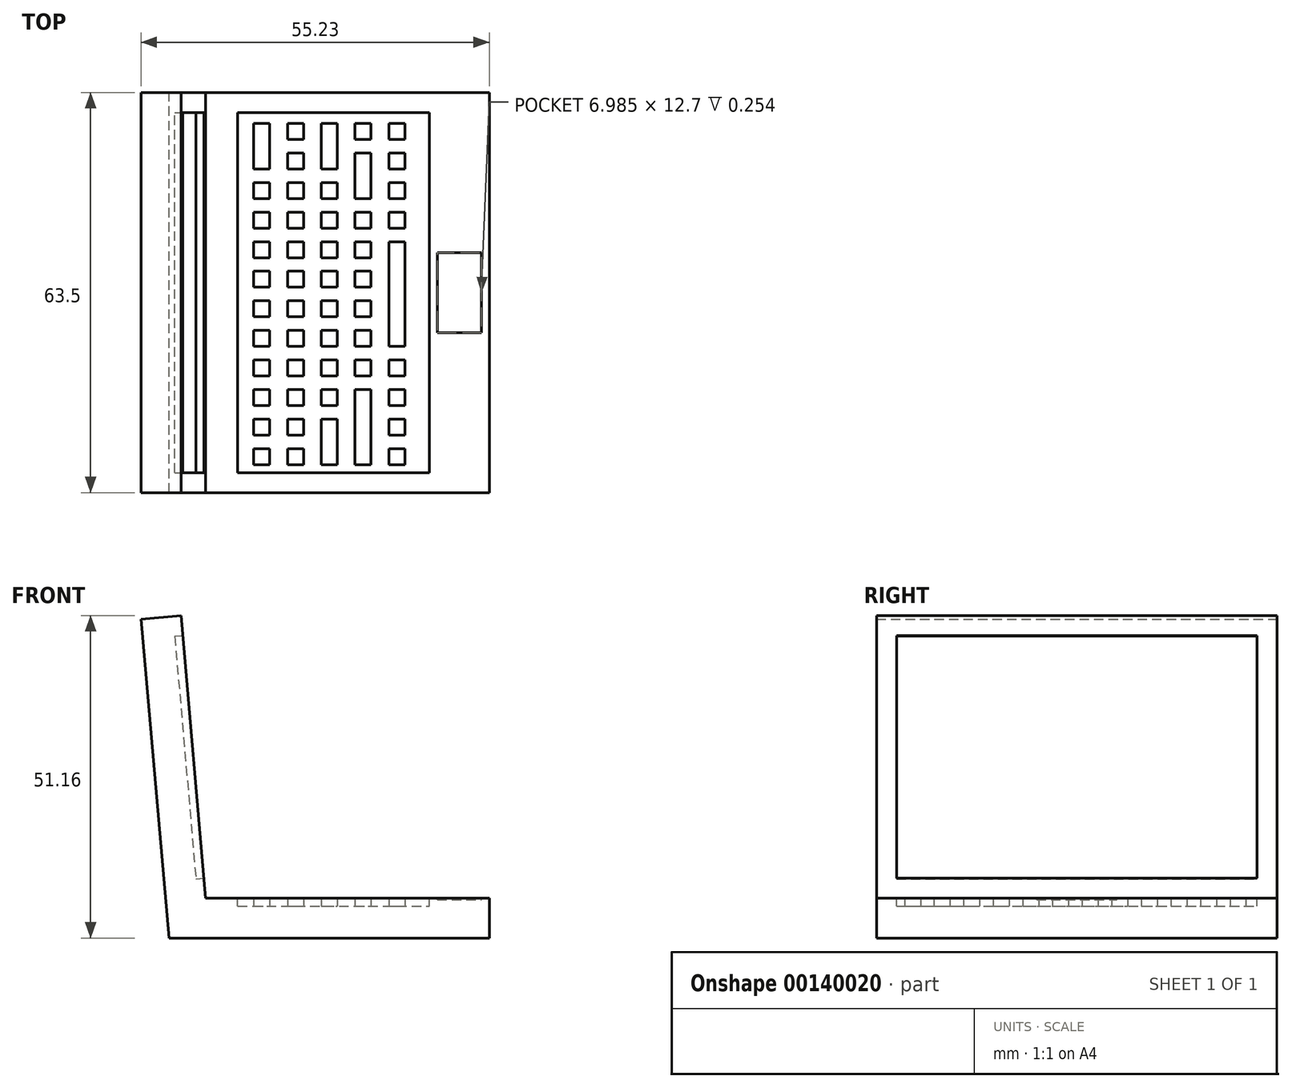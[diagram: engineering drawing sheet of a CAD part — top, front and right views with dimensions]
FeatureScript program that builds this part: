
annotation { "Feature Type Name" : "Feature", "Feature Type Description" : "" }
export const myFeature = defineFeature(function(context is Context, id is Id, definition is map)
    precondition{}
    {
        {
            var Q0;
            Q0=qCreatedBy(makeId("Front.planeOp"),FACE);
            var sketch = newSketch(context, id + "F0", { "sketchPlane" : qUnion([Q0])});
            skLineSegment(sketch, "E0", {"start": v(-10.25, 44.26) * mm, "end": v(-5.82, -6.35) * mm});
            skLineSegment(sketch, "E1", {"start": v(-5.82, -6.35) * mm, "end": v(44.98, -6.35) * mm});
            skLineSegment(sketch, "E2", {"start": v(44.98, -6.35) * mm, "end": v(44.98, 0) * mm});
            skLineSegment(sketch, "E3", {"start": v(44.98, 0) * mm, "end": v(0, 0) * mm});
            skLineSegment(sketch, "E4", {"start": v(0, 0) * mm, "end": v(-3.92, 44.81) * mm});
            skLineSegment(sketch, "E5", {"start": v(-3.92, 44.81) * mm, "end": v(-10.25, 44.26) * mm});
            skSolve(sketch);
        }
        {
            var Q0;
            Q0=makeQuery(id+"F0.imprint","IMPRINT",FACE,{"disambiguationData":[TD([[makeQuery(id+"F0.imprint","IMPRINT",EDGE,{"derivedFrom":sQuery(id+"F0.wireOp",EDGE,"E0")}),1.0]])]});
            extrude(context, id + "F1", {"entities" : qUnion([Q0]), "depth" : 31.75 * mm, "hasSecondDirection" : true, "secondDirectionOppositeDirection" : true, "secondDirectionDepth" : 31.75 * mm});
        }
        {
            var Q0;
            Q0=makeQuery(id+"F1.opExtrude","SWEPT_FACE",FACE,{"disambiguationData":[OSD([sQuery(id+"F0.wireOp",EDGE,"E3")])]});
            var sketch = newSketch(context, id + "F2", { "sketchPlane" : qUnion([Q0])});
            skLineSegment(sketch, "E6.bottom", {"start": v(5.08, -28.57) * mm, "end": v(35.46, -28.57) * mm});
            skLineSegment(sketch, "E6.top", {"start": v(5.08, 28.57) * mm, "end": v(35.46, 28.57) * mm});
            skLineSegment(sketch, "E6.left", {"start": v(5.08, -28.57) * mm, "end": v(5.08, 28.57) * mm});
            skLineSegment(sketch, "E6.right", {"start": v(35.46, -28.57) * mm, "end": v(35.46, 28.57) * mm});
            skPoint(sketch, "E7", {"position": v(5.08, 0) * mm});
            skSolve(sketch);
        }
        {
            var Q0;
            Q0 = qSketchRegion(id + "F2", true);
            extrude(context, id + "F3", {"entities" : qUnion([Q0]), "operationType" : NewBodyOperationType.REMOVE, "oppositeDirection" : true, "depth" : 1.27 * mm});
        }
        {
            var Q0;
            Q0=makeQuery(id+"F1.opExtrude","SWEPT_FACE",FACE,{"disambiguationData":[OSD([sQuery(id+"F0.wireOp",EDGE,"E4")])]});
            var sketch = newSketch(context, id + "F4", { "sketchPlane" : qUnion([Q0])});
            skLineSegment(sketch, "E8.bottom", {"start": v(-28.57, 41.8) * mm, "end": v(28.57, 41.8) * mm});
            skLineSegment(sketch, "E8.top", {"start": v(-28.57, 3.17) * mm, "end": v(28.57, 3.17) * mm});
            skLineSegment(sketch, "E8.left", {"start": v(-28.57, 41.8) * mm, "end": v(-28.57, 3.17) * mm});
            skLineSegment(sketch, "E8.right", {"start": v(28.57, 41.8) * mm, "end": v(28.57, 3.18) * mm});
            skPoint(sketch, "E9", {"position": v(0, 41.8) * mm});
            skSolve(sketch);
        }
        {
            var Q0;
            Q0=makeQuery(id+"F4.imprint","IMPRINT",FACE,{"disambiguationData":[TD([[makeQuery(id+"F4.imprint","IMPRINT",EDGE,{"derivedFrom":sQuery(id+"F4.wireOp",EDGE,"E8.bottom")}),-1.0]])]});
            extrude(context, id + "F5", {"entities" : qUnion([Q0]), "operationType" : NewBodyOperationType.REMOVE, "oppositeDirection" : true, "depth" : 1.27 * mm});
        }
        {
            var Q0;
            Q0=makeQuery(id+"F3.boolean.opBoolean","COPY",FACE,{"derivedFrom":makeQuery(id+"F3.opExtrude","CAP_FACE",FACE,{"disambiguationData":[OSD([sQuery(id+"F2.wireOp",EDGE,"E6.bottom"),sQuery(id+"F2.wireOp",EDGE,"E6.top"),sQuery(id+"F2.wireOp",EDGE,"E6.left"),sQuery(id+"F2.wireOp",EDGE,"E6.right")])],"isStart":false})});
            var sketch = newSketch(context, id + "F6", { "sketchPlane" : qUnion([Q0])});
            skLineSegment(sketch, "E10.bottom", {"start": v(7.62, -27.3) * mm, "end": v(10.16, -27.3) * mm});
            skLineSegment(sketch, "E10.top", {"start": v(7.62, -24.76) * mm, "end": v(10.16, -24.76) * mm});
            skLineSegment(sketch, "E10.left", {"start": v(7.62, -27.3) * mm, "end": v(7.62, -24.76) * mm});
            skLineSegment(sketch, "E10.right", {"start": v(10.16, -27.3) * mm, "end": v(10.16, -24.77) * mm});
            skLineSegment(sketch, "E11.0.1.0", {"start": v(10.16, -22.61) * mm, "end": v(10.16, -20.07) * mm});
            skLineSegment(sketch, "E11.0.1.1", {"start": v(7.62, -22.61) * mm, "end": v(7.62, -20.07) * mm});
            skLineSegment(sketch, "E11.0.1.2", {"start": v(7.62, -20.07) * mm, "end": v(10.16, -20.07) * mm});
            skLineSegment(sketch, "E11.0.1.3", {"start": v(7.62, -22.61) * mm, "end": v(10.16, -22.61) * mm});
            skLineSegment(sketch, "E11.0.2.0", {"start": v(10.16, -17.92) * mm, "end": v(10.16, -15.38) * mm});
            skLineSegment(sketch, "E11.0.2.1", {"start": v(7.62, -17.92) * mm, "end": v(7.62, -15.38) * mm});
            skLineSegment(sketch, "E11.0.2.2", {"start": v(7.62, -15.38) * mm, "end": v(10.16, -15.38) * mm});
            skLineSegment(sketch, "E11.0.2.3", {"start": v(7.62, -17.92) * mm, "end": v(10.16, -17.92) * mm});
            skLineSegment(sketch, "E11.0.3.0", {"start": v(10.16, -13.23) * mm, "end": v(10.16, -10.69) * mm});
            skLineSegment(sketch, "E11.0.3.1", {"start": v(7.62, -13.23) * mm, "end": v(7.62, -10.69) * mm});
            skLineSegment(sketch, "E11.0.3.2", {"start": v(7.62, -10.69) * mm, "end": v(10.16, -10.69) * mm});
            skLineSegment(sketch, "E11.0.3.3", {"start": v(7.62, -13.23) * mm, "end": v(10.16, -13.23) * mm});
            skLineSegment(sketch, "E11.0.4.0", {"start": v(10.16, -8.53) * mm, "end": v(10.16, -6) * mm});
            skLineSegment(sketch, "E11.0.4.1", {"start": v(7.62, -8.53) * mm, "end": v(7.62, -6) * mm});
            skLineSegment(sketch, "E11.0.4.2", {"start": v(7.62, -6) * mm, "end": v(10.16, -6) * mm});
            skLineSegment(sketch, "E11.0.4.3", {"start": v(7.62, -8.53) * mm, "end": v(10.16, -8.53) * mm});
            skLineSegment(sketch, "E11.0.5.0", {"start": v(10.16, -3.84) * mm, "end": v(10.16, -1.3) * mm});
            skLineSegment(sketch, "E11.0.5.1", {"start": v(7.62, -3.84) * mm, "end": v(7.62, -1.3) * mm});
            skLineSegment(sketch, "E11.0.5.2", {"start": v(7.62, -1.3) * mm, "end": v(10.16, -1.3) * mm});
            skLineSegment(sketch, "E11.0.5.3", {"start": v(7.62, -3.84) * mm, "end": v(10.16, -3.84) * mm});
            skLineSegment(sketch, "E11.0.6.0", {"start": v(10.16, 0.85) * mm, "end": v(10.16, 3.4) * mm});
            skLineSegment(sketch, "E11.0.6.1", {"start": v(7.62, 0.85) * mm, "end": v(7.62, 3.4) * mm});
            skLineSegment(sketch, "E11.0.6.2", {"start": v(7.62, 3.4) * mm, "end": v(10.16, 3.4) * mm});
            skLineSegment(sketch, "E11.0.6.3", {"start": v(7.62, 0.85) * mm, "end": v(10.16, 0.85) * mm});
            skLineSegment(sketch, "E11.0.7.0", {"start": v(10.16, 5.54) * mm, "end": v(10.16, 8.08) * mm});
            skLineSegment(sketch, "E11.0.7.1", {"start": v(7.62, 5.54) * mm, "end": v(7.62, 8.08) * mm});
            skLineSegment(sketch, "E11.0.7.2", {"start": v(7.62, 8.08) * mm, "end": v(10.16, 8.08) * mm});
            skLineSegment(sketch, "E11.0.7.3", {"start": v(7.62, 5.54) * mm, "end": v(10.16, 5.54) * mm});
            skLineSegment(sketch, "E11.0.8.0", {"start": v(10.16, 10.24) * mm, "end": v(10.16, 12.78) * mm});
            skLineSegment(sketch, "E11.0.8.1", {"start": v(7.62, 10.24) * mm, "end": v(7.62, 12.78) * mm});
            skLineSegment(sketch, "E11.0.8.2", {"start": v(7.62, 12.78) * mm, "end": v(10.16, 12.78) * mm});
            skLineSegment(sketch, "E11.0.8.3", {"start": v(7.62, 10.24) * mm, "end": v(10.16, 10.24) * mm});
            skLineSegment(sketch, "E11.0.9.0", {"start": v(10.16, 14.93) * mm, "end": v(10.16, 17.47) * mm});
            skLineSegment(sketch, "E11.0.9.1", {"start": v(7.62, 14.93) * mm, "end": v(7.62, 17.47) * mm});
            skLineSegment(sketch, "E11.0.9.2", {"start": v(7.62, 17.47) * mm, "end": v(10.16, 17.47) * mm});
            skLineSegment(sketch, "E11.0.9.3", {"start": v(7.62, 14.93) * mm, "end": v(10.16, 14.93) * mm});
            skLineSegment(sketch, "E11.0.10.0", {"start": v(10.16, 19.62) * mm, "end": v(10.16, 22.16) * mm});
            skLineSegment(sketch, "E11.0.10.1", {"start": v(7.62, 19.62) * mm, "end": v(7.62, 22.16) * mm});
            skLineSegment(sketch, "E11.0.10.3", {"start": v(7.62, 19.62) * mm, "end": v(10.16, 19.62) * mm});
            skLineSegment(sketch, "E11.0.11.0", {"start": v(10.16, 24.31) * mm, "end": v(10.16, 26.85) * mm});
            skLineSegment(sketch, "E11.0.11.1", {"start": v(7.62, 24.31) * mm, "end": v(7.62, 26.85) * mm});
            skLineSegment(sketch, "E11.0.11.2", {"start": v(7.62, 26.85) * mm, "end": v(10.16, 26.85) * mm});
            skLineSegment(sketch, "E11.1.0.0", {"start": v(15.52, -27.3) * mm, "end": v(15.52, -24.77) * mm});
            skLineSegment(sketch, "E11.1.0.1", {"start": v(12.98, -27.3) * mm, "end": v(12.98, -24.76) * mm});
            skLineSegment(sketch, "E11.1.0.2", {"start": v(12.98, -24.76) * mm, "end": v(15.52, -24.76) * mm});
            skLineSegment(sketch, "E11.1.0.3", {"start": v(12.98, -27.3) * mm, "end": v(15.52, -27.3) * mm});
            skLineSegment(sketch, "E11.1.1.0", {"start": v(15.52, -22.61) * mm, "end": v(15.52, -20.07) * mm});
            skLineSegment(sketch, "E11.1.1.1", {"start": v(12.98, -22.61) * mm, "end": v(12.98, -20.07) * mm});
            skLineSegment(sketch, "E11.1.1.2", {"start": v(12.98, -20.07) * mm, "end": v(15.52, -20.07) * mm});
            skLineSegment(sketch, "E11.1.1.3", {"start": v(12.98, -22.61) * mm, "end": v(15.52, -22.61) * mm});
            skLineSegment(sketch, "E11.1.2.0", {"start": v(15.52, -17.92) * mm, "end": v(15.52, -15.38) * mm});
            skLineSegment(sketch, "E11.1.2.1", {"start": v(12.98, -17.92) * mm, "end": v(12.98, -15.38) * mm});
            skLineSegment(sketch, "E11.1.2.2", {"start": v(12.98, -15.38) * mm, "end": v(15.52, -15.38) * mm});
            skLineSegment(sketch, "E11.1.2.3", {"start": v(12.98, -17.92) * mm, "end": v(15.52, -17.92) * mm});
            skLineSegment(sketch, "E11.1.3.0", {"start": v(15.52, -13.23) * mm, "end": v(15.52, -10.69) * mm});
            skLineSegment(sketch, "E11.1.3.1", {"start": v(12.98, -13.23) * mm, "end": v(12.98, -10.69) * mm});
            skLineSegment(sketch, "E11.1.3.2", {"start": v(12.98, -10.69) * mm, "end": v(15.52, -10.69) * mm});
            skLineSegment(sketch, "E11.1.3.3", {"start": v(12.98, -13.23) * mm, "end": v(15.52, -13.23) * mm});
            skLineSegment(sketch, "E11.1.4.0", {"start": v(15.52, -8.53) * mm, "end": v(15.52, -6) * mm});
            skLineSegment(sketch, "E11.1.4.1", {"start": v(12.98, -8.53) * mm, "end": v(12.98, -6) * mm});
            skLineSegment(sketch, "E11.1.4.2", {"start": v(12.98, -6) * mm, "end": v(15.52, -6) * mm});
            skLineSegment(sketch, "E11.1.4.3", {"start": v(12.98, -8.53) * mm, "end": v(15.52, -8.53) * mm});
            skLineSegment(sketch, "E11.1.5.0", {"start": v(15.52, -3.84) * mm, "end": v(15.52, -1.3) * mm});
            skLineSegment(sketch, "E11.1.5.1", {"start": v(12.98, -3.84) * mm, "end": v(12.98, -1.3) * mm});
            skLineSegment(sketch, "E11.1.5.2", {"start": v(12.98, -1.3) * mm, "end": v(15.52, -1.3) * mm});
            skLineSegment(sketch, "E11.1.5.3", {"start": v(12.98, -3.84) * mm, "end": v(15.52, -3.84) * mm});
            skLineSegment(sketch, "E11.1.6.0", {"start": v(15.52, 0.85) * mm, "end": v(15.52, 3.4) * mm});
            skLineSegment(sketch, "E11.1.6.1", {"start": v(12.98, 0.85) * mm, "end": v(12.98, 3.4) * mm});
            skLineSegment(sketch, "E11.1.6.2", {"start": v(12.98, 3.4) * mm, "end": v(15.52, 3.4) * mm});
            skLineSegment(sketch, "E11.1.6.3", {"start": v(12.98, 0.85) * mm, "end": v(15.52, 0.85) * mm});
            skLineSegment(sketch, "E11.1.7.0", {"start": v(15.52, 5.54) * mm, "end": v(15.52, 8.08) * mm});
            skLineSegment(sketch, "E11.1.7.1", {"start": v(12.98, 5.54) * mm, "end": v(12.98, 8.08) * mm});
            skLineSegment(sketch, "E11.1.7.2", {"start": v(12.98, 8.08) * mm, "end": v(15.52, 8.08) * mm});
            skLineSegment(sketch, "E11.1.7.3", {"start": v(12.98, 5.54) * mm, "end": v(15.52, 5.54) * mm});
            skLineSegment(sketch, "E11.1.8.0", {"start": v(15.52, 10.24) * mm, "end": v(15.52, 12.78) * mm});
            skLineSegment(sketch, "E11.1.8.1", {"start": v(12.98, 10.24) * mm, "end": v(12.98, 12.78) * mm});
            skLineSegment(sketch, "E11.1.8.2", {"start": v(12.98, 12.78) * mm, "end": v(15.52, 12.78) * mm});
            skLineSegment(sketch, "E11.1.8.3", {"start": v(12.98, 10.24) * mm, "end": v(15.52, 10.24) * mm});
            skLineSegment(sketch, "E11.1.9.0", {"start": v(15.52, 14.93) * mm, "end": v(15.52, 17.47) * mm});
            skLineSegment(sketch, "E11.1.9.1", {"start": v(12.98, 14.93) * mm, "end": v(12.98, 17.47) * mm});
            skLineSegment(sketch, "E11.1.9.2", {"start": v(12.98, 17.47) * mm, "end": v(15.52, 17.47) * mm});
            skLineSegment(sketch, "E11.1.9.3", {"start": v(12.98, 14.93) * mm, "end": v(15.52, 14.93) * mm});
            skLineSegment(sketch, "E11.1.10.0", {"start": v(15.52, 19.62) * mm, "end": v(15.52, 22.16) * mm});
            skLineSegment(sketch, "E11.1.10.1", {"start": v(12.98, 19.62) * mm, "end": v(12.98, 22.16) * mm});
            skLineSegment(sketch, "E11.1.10.2", {"start": v(12.98, 22.16) * mm, "end": v(15.52, 22.16) * mm});
            skLineSegment(sketch, "E11.1.10.3", {"start": v(12.98, 19.62) * mm, "end": v(15.52, 19.62) * mm});
            skLineSegment(sketch, "E11.1.11.0", {"start": v(15.52, 24.31) * mm, "end": v(15.52, 26.85) * mm});
            skLineSegment(sketch, "E11.1.11.1", {"start": v(12.98, 24.31) * mm, "end": v(12.98, 26.85) * mm});
            skLineSegment(sketch, "E11.1.11.2", {"start": v(12.98, 26.85) * mm, "end": v(15.52, 26.85) * mm});
            skLineSegment(sketch, "E11.1.11.3", {"start": v(12.98, 24.31) * mm, "end": v(15.52, 24.31) * mm});
            skLineSegment(sketch, "E11.2.0.0", {"start": v(20.87, -27.3) * mm, "end": v(20.87, -24.77) * mm});
            skLineSegment(sketch, "E11.2.0.1", {"start": v(18.33, -27.3) * mm, "end": v(18.33, -24.76) * mm});
            skLineSegment(sketch, "E11.2.0.3", {"start": v(18.33, -27.3) * mm, "end": v(20.87, -27.3) * mm});
            skLineSegment(sketch, "E11.2.1.0", {"start": v(20.87, -22.61) * mm, "end": v(20.87, -20.07) * mm});
            skLineSegment(sketch, "E11.2.1.1", {"start": v(18.33, -22.61) * mm, "end": v(18.33, -20.07) * mm});
            skLineSegment(sketch, "E11.2.1.2", {"start": v(18.33, -20.07) * mm, "end": v(20.87, -20.07) * mm});
            skLineSegment(sketch, "E11.2.2.0", {"start": v(20.87, -17.92) * mm, "end": v(20.87, -15.38) * mm});
            skLineSegment(sketch, "E11.2.2.1", {"start": v(18.33, -17.92) * mm, "end": v(18.33, -15.38) * mm});
            skLineSegment(sketch, "E11.2.2.2", {"start": v(18.33, -15.38) * mm, "end": v(20.87, -15.38) * mm});
            skLineSegment(sketch, "E11.2.2.3", {"start": v(18.33, -17.92) * mm, "end": v(20.87, -17.92) * mm});
            skLineSegment(sketch, "E11.2.3.0", {"start": v(20.87, -13.23) * mm, "end": v(20.87, -10.69) * mm});
            skLineSegment(sketch, "E11.2.3.1", {"start": v(18.33, -13.23) * mm, "end": v(18.33, -10.69) * mm});
            skLineSegment(sketch, "E11.2.3.2", {"start": v(18.33, -10.69) * mm, "end": v(20.87, -10.69) * mm});
            skLineSegment(sketch, "E11.2.3.3", {"start": v(18.33, -13.23) * mm, "end": v(20.87, -13.23) * mm});
            skLineSegment(sketch, "E11.2.4.0", {"start": v(20.87, -8.53) * mm, "end": v(20.87, -6) * mm});
            skLineSegment(sketch, "E11.2.4.1", {"start": v(18.33, -8.53) * mm, "end": v(18.33, -6) * mm});
            skLineSegment(sketch, "E11.2.4.2", {"start": v(18.33, -6) * mm, "end": v(20.87, -6) * mm});
            skLineSegment(sketch, "E11.2.4.3", {"start": v(18.33, -8.53) * mm, "end": v(20.87, -8.53) * mm});
            skLineSegment(sketch, "E11.2.5.0", {"start": v(20.87, -3.84) * mm, "end": v(20.87, -1.3) * mm});
            skLineSegment(sketch, "E11.2.5.1", {"start": v(18.33, -3.84) * mm, "end": v(18.33, -1.3) * mm});
            skLineSegment(sketch, "E11.2.5.2", {"start": v(18.33, -1.3) * mm, "end": v(20.87, -1.3) * mm});
            skLineSegment(sketch, "E11.2.5.3", {"start": v(18.33, -3.84) * mm, "end": v(20.87, -3.84) * mm});
            skLineSegment(sketch, "E11.2.6.0", {"start": v(20.87, 0.85) * mm, "end": v(20.87, 3.4) * mm});
            skLineSegment(sketch, "E11.2.6.1", {"start": v(18.33, 0.85) * mm, "end": v(18.33, 3.4) * mm});
            skLineSegment(sketch, "E11.2.6.2", {"start": v(18.33, 3.4) * mm, "end": v(20.87, 3.4) * mm});
            skLineSegment(sketch, "E11.2.6.3", {"start": v(18.33, 0.85) * mm, "end": v(20.87, 0.85) * mm});
            skLineSegment(sketch, "E11.2.7.0", {"start": v(20.87, 5.54) * mm, "end": v(20.87, 8.08) * mm});
            skLineSegment(sketch, "E11.2.7.1", {"start": v(18.33, 5.54) * mm, "end": v(18.33, 8.08) * mm});
            skLineSegment(sketch, "E11.2.7.2", {"start": v(18.33, 8.08) * mm, "end": v(20.87, 8.08) * mm});
            skLineSegment(sketch, "E11.2.7.3", {"start": v(18.33, 5.54) * mm, "end": v(20.87, 5.54) * mm});
            skLineSegment(sketch, "E11.2.8.0", {"start": v(20.87, 10.24) * mm, "end": v(20.87, 12.78) * mm});
            skLineSegment(sketch, "E11.2.8.1", {"start": v(18.33, 10.24) * mm, "end": v(18.33, 12.78) * mm});
            skLineSegment(sketch, "E11.2.8.2", {"start": v(18.33, 12.78) * mm, "end": v(20.87, 12.78) * mm});
            skLineSegment(sketch, "E11.2.8.3", {"start": v(18.33, 10.24) * mm, "end": v(20.87, 10.24) * mm});
            skLineSegment(sketch, "E11.2.9.0", {"start": v(20.87, 14.93) * mm, "end": v(20.87, 17.47) * mm});
            skLineSegment(sketch, "E11.2.9.1", {"start": v(18.33, 14.93) * mm, "end": v(18.33, 17.47) * mm});
            skLineSegment(sketch, "E11.2.9.2", {"start": v(18.33, 17.47) * mm, "end": v(20.87, 17.47) * mm});
            skLineSegment(sketch, "E11.2.9.3", {"start": v(18.33, 14.93) * mm, "end": v(20.87, 14.93) * mm});
            skLineSegment(sketch, "E11.2.10.0", {"start": v(20.87, 19.62) * mm, "end": v(20.87, 22.16) * mm});
            skLineSegment(sketch, "E11.2.10.1", {"start": v(18.33, 19.62) * mm, "end": v(18.33, 22.16) * mm});
            skLineSegment(sketch, "E11.2.10.3", {"start": v(18.33, 19.62) * mm, "end": v(20.87, 19.62) * mm});
            skLineSegment(sketch, "E11.2.11.0", {"start": v(20.87, 24.31) * mm, "end": v(20.87, 26.85) * mm});
            skLineSegment(sketch, "E11.2.11.1", {"start": v(18.33, 24.31) * mm, "end": v(18.33, 26.85) * mm});
            skLineSegment(sketch, "E11.2.11.2", {"start": v(18.33, 26.85) * mm, "end": v(20.87, 26.85) * mm});
            skLineSegment(sketch, "E11.3.0.0", {"start": v(26.23, -27.3) * mm, "end": v(26.23, -24.77) * mm});
            skLineSegment(sketch, "E11.3.0.1", {"start": v(23.69, -27.3) * mm, "end": v(23.69, -24.76) * mm});
            skLineSegment(sketch, "E11.3.0.3", {"start": v(23.69, -27.3) * mm, "end": v(26.23, -27.3) * mm});
            skLineSegment(sketch, "E11.3.1.0", {"start": v(26.23, -22.61) * mm, "end": v(26.23, -20.07) * mm});
            skLineSegment(sketch, "E11.3.1.1", {"start": v(23.69, -22.61) * mm, "end": v(23.69, -20.07) * mm});
            skLineSegment(sketch, "E11.3.2.0", {"start": v(26.23, -17.92) * mm, "end": v(26.23, -15.38) * mm});
            skLineSegment(sketch, "E11.3.2.1", {"start": v(23.69, -17.92) * mm, "end": v(23.69, -15.38) * mm});
            skLineSegment(sketch, "E11.3.2.2", {"start": v(23.69, -15.38) * mm, "end": v(26.23, -15.38) * mm});
            skLineSegment(sketch, "E11.3.3.0", {"start": v(26.23, -13.23) * mm, "end": v(26.23, -10.69) * mm});
            skLineSegment(sketch, "E11.3.3.1", {"start": v(23.69, -13.23) * mm, "end": v(23.69, -10.69) * mm});
            skLineSegment(sketch, "E11.3.3.2", {"start": v(23.69, -10.69) * mm, "end": v(26.23, -10.69) * mm});
            skLineSegment(sketch, "E11.3.3.3", {"start": v(23.69, -13.23) * mm, "end": v(26.23, -13.23) * mm});
            skLineSegment(sketch, "E11.3.4.0", {"start": v(26.23, -8.53) * mm, "end": v(26.23, -6) * mm});
            skLineSegment(sketch, "E11.3.4.1", {"start": v(23.69, -8.53) * mm, "end": v(23.69, -6) * mm});
            skLineSegment(sketch, "E11.3.4.2", {"start": v(23.69, -6) * mm, "end": v(26.23, -6) * mm});
            skLineSegment(sketch, "E11.3.4.3", {"start": v(23.69, -8.53) * mm, "end": v(26.23, -8.53) * mm});
            skLineSegment(sketch, "E11.3.5.0", {"start": v(26.23, -3.84) * mm, "end": v(26.23, -1.3) * mm});
            skLineSegment(sketch, "E11.3.5.1", {"start": v(23.69, -3.84) * mm, "end": v(23.69, -1.3) * mm});
            skLineSegment(sketch, "E11.3.5.2", {"start": v(23.69, -1.3) * mm, "end": v(26.23, -1.3) * mm});
            skLineSegment(sketch, "E11.3.5.3", {"start": v(23.69, -3.84) * mm, "end": v(26.23, -3.84) * mm});
            skLineSegment(sketch, "E11.3.6.0", {"start": v(26.23, 0.85) * mm, "end": v(26.23, 3.4) * mm});
            skLineSegment(sketch, "E11.3.6.1", {"start": v(23.69, 0.85) * mm, "end": v(23.69, 3.4) * mm});
            skLineSegment(sketch, "E11.3.6.2", {"start": v(23.69, 3.4) * mm, "end": v(26.23, 3.4) * mm});
            skLineSegment(sketch, "E11.3.6.3", {"start": v(23.69, 0.85) * mm, "end": v(26.23, 0.85) * mm});
            skLineSegment(sketch, "E11.3.7.0", {"start": v(26.23, 5.54) * mm, "end": v(26.23, 8.08) * mm});
            skLineSegment(sketch, "E11.3.7.1", {"start": v(23.69, 5.54) * mm, "end": v(23.69, 8.08) * mm});
            skLineSegment(sketch, "E11.3.7.2", {"start": v(23.69, 8.08) * mm, "end": v(26.23, 8.08) * mm});
            skLineSegment(sketch, "E11.3.7.3", {"start": v(23.69, 5.54) * mm, "end": v(26.23, 5.54) * mm});
            skLineSegment(sketch, "E11.3.8.0", {"start": v(26.23, 10.24) * mm, "end": v(26.23, 12.78) * mm});
            skLineSegment(sketch, "E11.3.8.1", {"start": v(23.69, 10.24) * mm, "end": v(23.69, 12.78) * mm});
            skLineSegment(sketch, "E11.3.8.2", {"start": v(23.69, 12.78) * mm, "end": v(26.23, 12.78) * mm});
            skLineSegment(sketch, "E11.3.8.3", {"start": v(23.69, 10.24) * mm, "end": v(26.23, 10.24) * mm});
            skLineSegment(sketch, "E11.3.9.0", {"start": v(26.23, 14.93) * mm, "end": v(26.23, 17.47) * mm});
            skLineSegment(sketch, "E11.3.9.1", {"start": v(23.69, 14.93) * mm, "end": v(23.69, 17.47) * mm});
            skLineSegment(sketch, "E11.3.9.3", {"start": v(23.69, 14.93) * mm, "end": v(26.23, 14.93) * mm});
            skLineSegment(sketch, "E11.3.10.0", {"start": v(26.23, 19.62) * mm, "end": v(26.23, 22.16) * mm});
            skLineSegment(sketch, "E11.3.10.1", {"start": v(23.69, 19.62) * mm, "end": v(23.69, 22.16) * mm});
            skLineSegment(sketch, "E11.3.10.2", {"start": v(23.69, 22.16) * mm, "end": v(26.23, 22.16) * mm});
            skLineSegment(sketch, "E11.3.11.0", {"start": v(26.23, 24.31) * mm, "end": v(26.23, 26.85) * mm});
            skLineSegment(sketch, "E11.3.11.1", {"start": v(23.69, 24.31) * mm, "end": v(23.69, 26.85) * mm});
            skLineSegment(sketch, "E11.3.11.2", {"start": v(23.69, 26.85) * mm, "end": v(26.23, 26.85) * mm});
            skLineSegment(sketch, "E11.3.11.3", {"start": v(23.69, 24.31) * mm, "end": v(26.23, 24.31) * mm});
            skLineSegment(sketch, "E11.4.0.0", {"start": v(31.59, -27.3) * mm, "end": v(31.59, -24.77) * mm});
            skLineSegment(sketch, "E11.4.0.1", {"start": v(29.05, -27.3) * mm, "end": v(29.05, -24.76) * mm});
            skLineSegment(sketch, "E11.4.0.2", {"start": v(29.05, -24.76) * mm, "end": v(31.59, -24.76) * mm});
            skLineSegment(sketch, "E11.4.0.3", {"start": v(29.05, -27.3) * mm, "end": v(31.59, -27.3) * mm});
            skLineSegment(sketch, "E11.4.1.0", {"start": v(31.59, -22.61) * mm, "end": v(31.59, -20.07) * mm});
            skLineSegment(sketch, "E11.4.1.1", {"start": v(29.05, -22.61) * mm, "end": v(29.05, -20.07) * mm});
            skLineSegment(sketch, "E11.4.1.2", {"start": v(29.05, -20.07) * mm, "end": v(31.59, -20.07) * mm});
            skLineSegment(sketch, "E11.4.1.3", {"start": v(29.05, -22.61) * mm, "end": v(31.59, -22.61) * mm});
            skLineSegment(sketch, "E11.4.2.0", {"start": v(31.59, -17.92) * mm, "end": v(31.59, -15.38) * mm});
            skLineSegment(sketch, "E11.4.2.1", {"start": v(29.05, -17.92) * mm, "end": v(29.05, -15.38) * mm});
            skLineSegment(sketch, "E11.4.2.2", {"start": v(29.05, -15.38) * mm, "end": v(31.59, -15.38) * mm});
            skLineSegment(sketch, "E11.4.2.3", {"start": v(29.05, -17.92) * mm, "end": v(31.59, -17.92) * mm});
            skLineSegment(sketch, "E11.4.3.0", {"start": v(31.59, -13.23) * mm, "end": v(31.59, -10.69) * mm});
            skLineSegment(sketch, "E11.4.3.1", {"start": v(29.05, -13.23) * mm, "end": v(29.05, -10.69) * mm});
            skLineSegment(sketch, "E11.4.3.2", {"start": v(29.05, -10.69) * mm, "end": v(31.59, -10.69) * mm});
            skLineSegment(sketch, "E11.4.3.3", {"start": v(29.05, -13.23) * mm, "end": v(31.59, -13.23) * mm});
            skLineSegment(sketch, "E11.4.8.0", {"start": v(31.59, 10.24) * mm, "end": v(31.59, 12.78) * mm});
            skLineSegment(sketch, "E11.4.8.1", {"start": v(29.05, 10.24) * mm, "end": v(29.05, 12.78) * mm});
            skLineSegment(sketch, "E11.4.8.2", {"start": v(29.05, 12.78) * mm, "end": v(31.59, 12.78) * mm});
            skLineSegment(sketch, "E11.4.8.3", {"start": v(29.05, 10.24) * mm, "end": v(31.59, 10.24) * mm});
            skLineSegment(sketch, "E11.4.9.0", {"start": v(31.59, 14.93) * mm, "end": v(31.59, 17.47) * mm});
            skLineSegment(sketch, "E11.4.9.1", {"start": v(29.05, 14.93) * mm, "end": v(29.05, 17.47) * mm});
            skLineSegment(sketch, "E11.4.9.2", {"start": v(29.05, 17.47) * mm, "end": v(31.59, 17.47) * mm});
            skLineSegment(sketch, "E11.4.9.3", {"start": v(29.05, 14.93) * mm, "end": v(31.59, 14.93) * mm});
            skLineSegment(sketch, "E11.4.10.0", {"start": v(31.59, 19.62) * mm, "end": v(31.59, 22.16) * mm});
            skLineSegment(sketch, "E11.4.10.1", {"start": v(29.05, 19.62) * mm, "end": v(29.05, 22.16) * mm});
            skLineSegment(sketch, "E11.4.10.2", {"start": v(29.05, 22.16) * mm, "end": v(31.59, 22.16) * mm});
            skLineSegment(sketch, "E11.4.10.3", {"start": v(29.05, 19.62) * mm, "end": v(31.59, 19.62) * mm});
            skLineSegment(sketch, "E11.4.11.0", {"start": v(31.59, 24.31) * mm, "end": v(31.59, 26.85) * mm});
            skLineSegment(sketch, "E11.4.11.1", {"start": v(29.05, 24.31) * mm, "end": v(29.05, 26.85) * mm});
            skLineSegment(sketch, "E11.4.11.2", {"start": v(29.05, 26.85) * mm, "end": v(31.59, 26.85) * mm});
            skLineSegment(sketch, "E11.4.11.3", {"start": v(29.05, 24.31) * mm, "end": v(31.59, 24.31) * mm});
            skLineSegment(sketch, "E11.direction1", {"start": v(7.62, -27.3) * mm, "end": v(12.98, -27.3) * mm, "construction": true});
            skLineSegment(sketch, "E11.direction2", {"start": v(7.62, -27.3) * mm, "end": v(7.62, -22.61) * mm, "construction": true});
            skLineSegment(sketch, "E12.bottom", {"start": v(29.05, -8.53) * mm, "end": v(31.59, -8.53) * mm});
            skLineSegment(sketch, "E12.top", {"start": v(29.05, 8.08) * mm, "end": v(31.59, 8.08) * mm});
            skLineSegment(sketch, "E12.left", {"start": v(29.05, -8.53) * mm, "end": v(29.05, 8.08) * mm});
            skLineSegment(sketch, "E12.right", {"start": v(31.59, -8.53) * mm, "end": v(31.59, 8.08) * mm});
            skLineSegment(sketch, "E13", {"start": v(18.33, 22.16) * mm, "end": v(18.33, 24.31) * mm});
            skLineSegment(sketch, "E14", {"start": v(20.87, 22.16) * mm, "end": v(20.87, 24.31) * mm});
            skLineSegment(sketch, "E15", {"start": v(23.69, 19.62) * mm, "end": v(23.69, 17.47) * mm});
            skLineSegment(sketch, "E16", {"start": v(26.23, 19.62) * mm, "end": v(26.23, 17.47) * mm});
            skLineSegment(sketch, "E17", {"start": v(7.62, 22.16) * mm, "end": v(7.62, 24.31) * mm});
            skLineSegment(sketch, "E18", {"start": v(10.16, 22.16) * mm, "end": v(10.16, 24.31) * mm});
            skLineSegment(sketch, "E19", {"start": v(18.33, -24.76) * mm, "end": v(18.33, -22.61) * mm});
            skLineSegment(sketch, "E20", {"start": v(20.87, -24.77) * mm, "end": v(20.87, -22.61) * mm});
            skLineSegment(sketch, "E21", {"start": v(23.69, -24.76) * mm, "end": v(23.69, -22.61) * mm});
            skLineSegment(sketch, "E22", {"start": v(26.23, -24.77) * mm, "end": v(26.23, -22.61) * mm});
            skLineSegment(sketch, "E23", {"start": v(23.69, -20.07) * mm, "end": v(23.69, -17.92) * mm});
            skLineSegment(sketch, "E24", {"start": v(26.23, -20.07) * mm, "end": v(26.23, -17.92) * mm});
            skSolve(sketch);
        }
        {
            var Q0;
            Q0 = qSketchRegion(id + "F6", true);
            extrude(context, id + "F7", {"entities" : qUnion([Q0]), "operationType" : NewBodyOperationType.ADD, "depth" : 1.27 * mm});
        }
        {
            var Q0;
            Q0=makeQuery(id+"F1.opExtrude","SWEPT_FACE",FACE,{"disambiguationData":[OSD([sQuery(id+"F0.wireOp",EDGE,"E3")])]});
            var sketch = newSketch(context, id + "F8", { "sketchPlane" : qUnion([Q0])});
            skLineSegment(sketch, "E25.bottom", {"start": v(36.73, -6.35) * mm, "end": v(43.71, -6.35) * mm});
            skLineSegment(sketch, "E25.top", {"start": v(36.73, 6.35) * mm, "end": v(43.71, 6.35) * mm});
            skLineSegment(sketch, "E25.left", {"start": v(36.73, -6.35) * mm, "end": v(36.73, 6.35) * mm});
            skLineSegment(sketch, "E25.right", {"start": v(43.71, -6.35) * mm, "end": v(43.71, 6.35) * mm});
            skPoint(sketch, "E26", {"position": v(36.73, 0) * mm});
            skSolve(sketch);
        }
        {
            var Q0;
            Q0=makeQuery(id+"F8.imprint","IMPRINT",FACE,{"disambiguationData":[TD([[makeQuery(id+"F8.imprint","IMPRINT",EDGE,{"derivedFrom":sQuery(id+"F8.wireOp",EDGE,"E25.bottom")}),1.0]])]});
            extrude(context, id + "F9", {"entities" : qUnion([Q0]), "operationType" : NewBodyOperationType.REMOVE, "oppositeDirection" : true, "depth" : 0.25 * mm});
        }
    });
